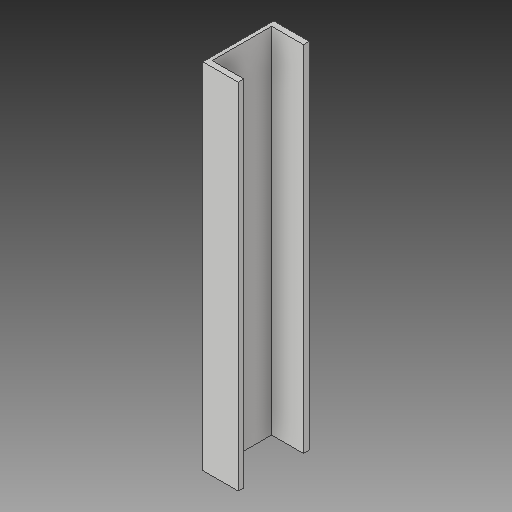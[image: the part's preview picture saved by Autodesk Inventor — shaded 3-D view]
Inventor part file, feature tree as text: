
AUTODESK INVENTOR PART (.ipt)
format: ipt  version: 2019 (Build 230136000, 136)  size: 88,064 bytes
history: native  units: in
note: dims shown in document units (in); Inventor stores cm internally (conversion verified against a paired STEP export)
features: other x3, sketch x1
ambient origin geometry x8: Origin, YZ Plane, XZ Plane, XY Plane, X Axis, Y Axis, Z Axis, Center Point
bodies: Solid1 (feature_tree)
feature tree (4):
  other  "Channel1_MIR2.ipt"
  other  "Solid1::Channel1_MIR2.ipt"
  other  "TaggingFeature1"
  sketch  "Sketch1"  dims[d0=0.3937in]
